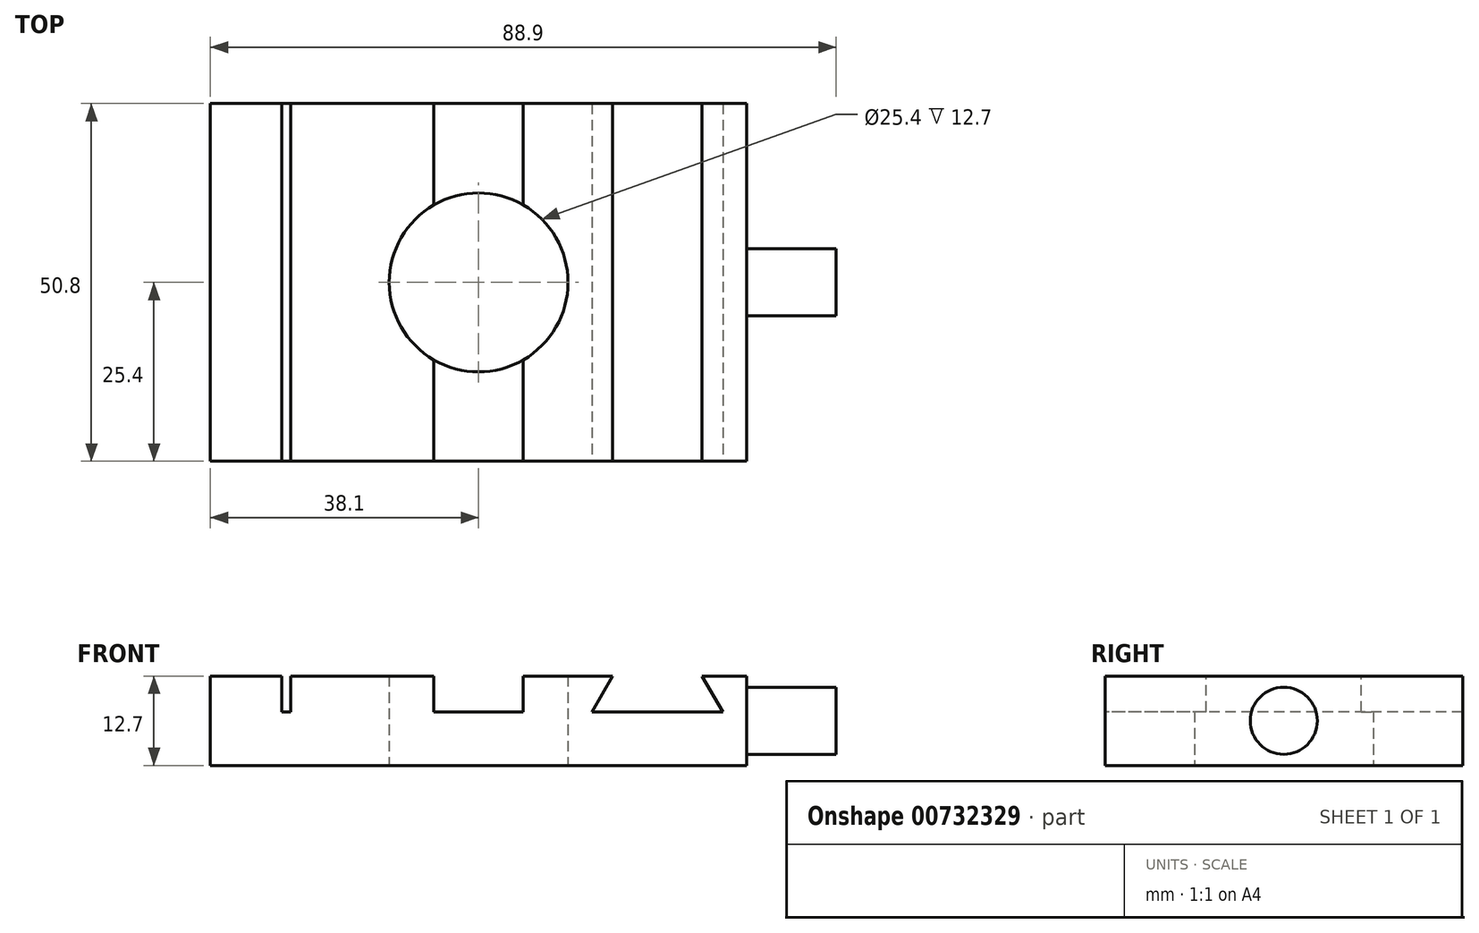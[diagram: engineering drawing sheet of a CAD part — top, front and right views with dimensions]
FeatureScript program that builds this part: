
annotation { "Feature Type Name" : "Feature", "Feature Type Description" : "" }
export const myFeature = defineFeature(function(context is Context, id is Id, definition is map)
    precondition{}
    {
        {
            var Q0;
            Q0=qCreatedBy(makeId("Top.planeOp"),FACE);
            var sketch = newSketch(context, id + "F0", { "sketchPlane" : qUnion([Q0])});
            skLineSegment(sketch, "E0.bottom", {"start": v(38.1, 25.4) * mm, "end": v(-38.1, 25.4) * mm});
            skLineSegment(sketch, "E0.top", {"start": v(38.1, -25.4) * mm, "end": v(-38.1, -25.4) * mm});
            skLineSegment(sketch, "E0.left", {"start": v(38.1, 25.4) * mm, "end": v(38.1, -25.4) * mm});
            skLineSegment(sketch, "E0.right", {"start": v(-38.1, 25.4) * mm, "end": v(-38.1, -25.4) * mm});
            skPoint(sketch, "E0.middle", {"position": v(0, 0) * mm});
            skCircle(sketch, "E1", {"center": v(0, 0) * mm, "radius": 12.7 * mm});
            skSolve(sketch);
        }
        {
            var Q0;
            Q0=makeQuery(id+"F0.imprint","IMPRINT",FACE,{"disambiguationData":[TD([[makeQuery(id+"F0.imprint","IMPRINT",EDGE,{"derivedFrom":sQuery(id+"F0.wireOp",EDGE,"E0.bottom")}),1.0]])]});
            extrude(context, id + "F1", {"entities" : qUnion([Q0]), "depth" : 12.7 * mm, "offsetDistance" : 25.4 * mm});
        }
        {
            var Q0;
            Q0=makeQuery(id+"F1.opExtrude","CAP_FACE",FACE,{"disambiguationData":[OSD([sQuery(id+"F0.wireOp",EDGE,"E0.bottom"),sQuery(id+"F0.wireOp",EDGE,"E0.top"),sQuery(id+"F0.wireOp",EDGE,"E0.left"),sQuery(id+"F0.wireOp",EDGE,"E0.right"),sQuery(id+"F0.wireOp",EDGE,"E1")])],"isStart":false});
            var sketch = newSketch(context, id + "F2", { "sketchPlane" : qUnion([Q0])});
            skLineSegment(sketch, "E2.bottom", {"start": v(-27.94, 25.4) * mm, "end": v(-26.67, 25.4) * mm});
            skLineSegment(sketch, "E2.top", {"start": v(-27.94, -25.4) * mm, "end": v(-26.67, -25.4) * mm});
            skLineSegment(sketch, "E2.left", {"start": v(-27.94, 25.4) * mm, "end": v(-27.94, -25.4) * mm});
            skLineSegment(sketch, "E2.right", {"start": v(-26.67, 25.4) * mm, "end": v(-26.67, -25.4) * mm});
            skLineSegment(sketch, "E3", {"start": v(-6.35, 25.4) * mm, "end": v(-6.35, -25.4) * mm});
            skLineSegment(sketch, "E4", {"start": v(-6.35, -25.4) * mm, "end": v(6.35, -25.4) * mm});
            skLineSegment(sketch, "E5", {"start": v(6.35, -25.4) * mm, "end": v(6.35, 25.4) * mm});
            skLineSegment(sketch, "E6", {"start": v(6.35, 25.4) * mm, "end": v(-6.35, 25.4) * mm});
            skLineSegment(sketch, "E7", {"start": v(0, 25.4) * mm, "end": v(0, -25.4) * mm, "construction": true});
            skSolve(sketch);
        }
        {
            var Q0;
            Q0=makeQuery(id+"F2.imprint","IMPRINT",FACE,{"disambiguationData":[TD([[makeQuery(id+"F2.imprint","IMPRINT",EDGE,{"derivedFrom":sQuery(id+"F2.wireOp",EDGE,"E2.bottom")}),1.0]])]});
            var Q1;
            {var subQ0=sQuery(id+"F2.wireOp",EDGE,"E4");Q1=makeQuery(id+"F2.imprint","IMPRINT",FACE,{"disambiguationData":[TD([[makeQuery(id+"F2.imprint","IMPRINT",EDGE,{"derivedFrom":subQ0}),-1.0]])]});}
            var Q2;
            {var subQ0=sQuery(id+"F2.wireOp",EDGE,"E6");Q2=makeQuery(id+"F2.imprint","IMPRINT",FACE,{"disambiguationData":[TD([[makeQuery(id+"F2.imprint","IMPRINT",EDGE,{"derivedFrom":subQ0}),1.0]])]});}
            extrude(context, id + "F3", {"entities" : qUnion([Q0, Q1, Q2]), "operationType" : NewBodyOperationType.REMOVE, "oppositeDirection" : true, "depth" : 5.08 * mm, "offsetDistance" : 25.4 * mm});
        }
        {
            var Q0;
            Q0=makeQuery(id+"F1.opExtrude","SWEPT_FACE",FACE,{"disambiguationData":[OSD([sQuery(id+"F0.wireOp",EDGE,"E0.top")])]});
            var sketch = newSketch(context, id + "F4", { "sketchPlane" : qUnion([Q0])});
            skLineSegment(sketch, "E8", {"start": v(19.05, 12.7) * mm, "end": v(16.12, 7.62) * mm});
            skLineSegment(sketch, "E9", {"start": v(16.12, 7.62) * mm, "end": v(34.68, 7.62) * mm});
            skLineSegment(sketch, "E10", {"start": v(34.68, 7.62) * mm, "end": v(31.75, 12.7) * mm});
            skLineSegment(sketch, "E11", {"start": v(31.75, 12.7) * mm, "end": v(19.05, 12.7) * mm});
            skLineSegment(sketch, "E12", {"start": v(25.4, 7.62) * mm, "end": v(25.4, 12.7) * mm, "construction": true});
            skSolve(sketch);
        }
        {
            var Q0;
            Q0=makeQuery(id+"F4.imprint","IMPRINT",FACE,{"disambiguationData":[TD([[makeQuery(id+"F4.imprint","IMPRINT",EDGE,{"derivedFrom":sQuery(id+"F4.wireOp",EDGE,"E8")}),1.0]])]});
            extrude(context, id + "F5", {"entities" : qUnion([Q0]), "operationType" : NewBodyOperationType.REMOVE, "endBound" : BoundingType.THROUGH_ALL, "oppositeDirection" : true, "depth" : 25.4 * mm, "offsetDistance" : 25.4 * mm});
        }
        {
            var Q0;
            Q0=makeQuery(id+"F1.opExtrude","SWEPT_FACE",FACE,{"disambiguationData":[OSD([sQuery(id+"F0.wireOp",EDGE,"E0.left")])]});
            var sketch = newSketch(context, id + "F6", { "sketchPlane" : qUnion([Q0])});
            skCircle(sketch, "E13", {"center": v(0, 6.35) * mm, "radius": 4.76 * mm});
            skPoint(sketch, "E13.centerSnap0", {"position": v(-25.4, 6.35) * mm});
            skPoint(sketch, "E13.centerSnap1", {"position": v(0, 12.7) * mm});
            skSolve(sketch);
        }
        {
            var Q0;
            Q0 = qSketchRegion(id + "F6", true);
            extrude(context, id + "F7", {"entities" : qUnion([Q0]), "operationType" : NewBodyOperationType.ADD, "depth" : 12.7 * mm, "offsetDistance" : 25.4 * mm});
        }
    });
